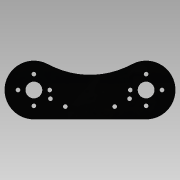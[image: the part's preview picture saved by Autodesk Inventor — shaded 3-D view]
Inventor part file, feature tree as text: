
AUTODESK INVENTOR PART (.ipt)
format: ipt  version: 2015 SP1 (Build 190203100, 203)  size: 126,464 bytes
history: native  units: mm
features: extrude x1, sketch x1
ambient origin geometry x8: Origin, YZ Plane, XZ Plane, XY Plane, X Axis, Y Axis, Z Axis, Center Point
bodies: Body1 (feature_tree)
feature tree (2):
  extrude  "Extrusion5"  Depth=5.0mm
  sketch  "Sketch1"  dims[d47=8.509mm d48=8.509mm d49=8.509mm d50=8.509mm d51=10.0mm d53=9.0mm d56=9.0mm d58=4.19811mm d72=50.0mm d74=3.21439mm d75=5.0mm d76=0.0mm]
